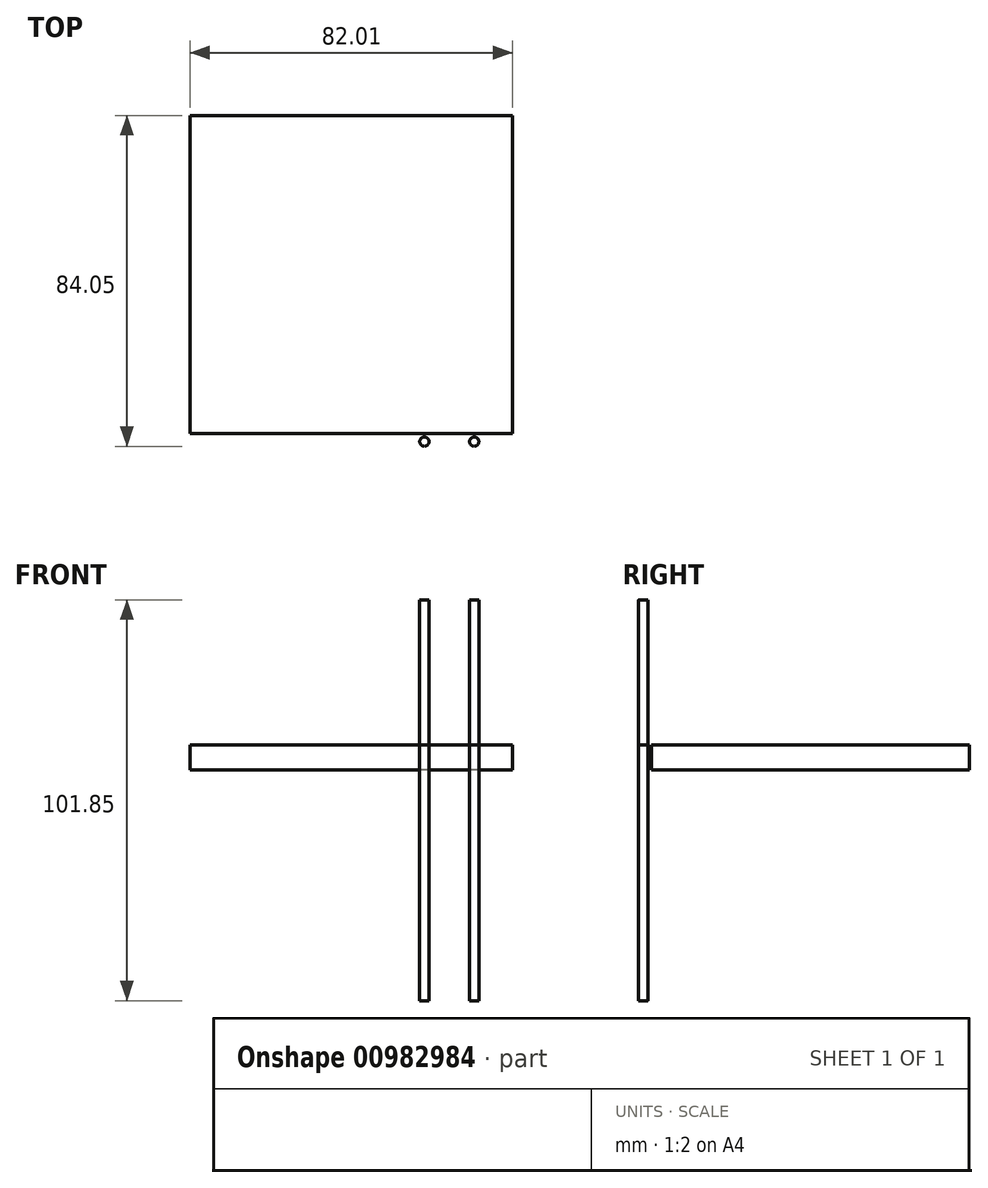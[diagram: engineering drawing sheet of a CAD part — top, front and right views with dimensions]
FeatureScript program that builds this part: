
annotation { "Feature Type Name" : "Feature", "Feature Type Description" : "" }
export const myFeature = defineFeature(function(context is Context, id is Id, definition is map)
    precondition{}
    {
        {
            var Q0;
            Q0=qCreatedBy(makeId("Top.planeOp"),FACE);
            var sketch = newSketch(context, id + "F0", { "sketchPlane" : qUnion([Q0])});
            skLineSegment(sketch, "E0.bottom", {"start": v(0, 0) * mm, "end": v(-82, 0) * mm});
            skLineSegment(sketch, "E0.top", {"start": v(0, 80.82) * mm, "end": v(-82, 80.82) * mm});
            skLineSegment(sketch, "E0.left", {"start": v(0, 0) * mm, "end": v(0, 80.82) * mm});
            skLineSegment(sketch, "E0.right", {"start": v(-82, 0) * mm, "end": v(-82, 80.82) * mm});
            skSolve(sketch);
        }
        {
            var Q0;
            Q0=makeQuery(id+"F0.imprint","IMPRINT",FACE,{"disambiguationData":[TD([[makeQuery(id+"F0.imprint","IMPRINT",EDGE,{"derivedFrom":sQuery(id+"F0.wireOp",EDGE,"E0.bottom")}),-1.0]])]});
            var sketch = newSketch(context, id + "F1", { "sketchPlane" : qUnion([Q0])});
            skCircle(sketch, "E1", {"center": v(-22.45, -2.05) * mm, "radius": 1.18 * mm});
            skCircle(sketch, "E2", {"center": v(-9.78, -2.05) * mm, "radius": 1.18 * mm});
            skSolve(sketch);
        }
        {
            var Q0;
            Q0=makeQuery(id+"F0.imprint","IMPRINT",FACE,{"disambiguationData":[TD([[makeQuery(id+"F0.imprint","IMPRINT",EDGE,{"derivedFrom":sQuery(id+"F0.wireOp",EDGE,"E0.bottom")}),-1.0]])]});
            var Q1;
            Q1=makeQuery(id+"F1.imprint","IMPRINT",FACE,{"disambiguationData":[TD([[makeQuery(id+"F1.imprint","IMPRINT",EDGE,{"derivedFrom":sQuery(id+"F1.wireOp",EDGE,"E2")}),1.0]])]});
            var Q2;
            Q2=makeQuery(id+"F1.imprint","IMPRINT",FACE,{"disambiguationData":[TD([[makeQuery(id+"F1.imprint","IMPRINT",EDGE,{"derivedFrom":sQuery(id+"F1.wireOp",EDGE,"E1")}),1.0]])]});
            extrude(context, id + "F2", {"entities" : qUnion([Q0, Q1, Q2]), "depth" : 65.02 * mm, "offsetDistance" : 25.4 * mm});
        }
        {
            var Q0;
            Q0=makeQuery(id+"F2.opExtrude","CAP_FACE",FACE,{"disambiguationData":[OSD([sQuery(id+"F0.wireOp",EDGE,"E0.bottom"),sQuery(id+"F0.wireOp",EDGE,"E0.top"),sQuery(id+"F0.wireOp",EDGE,"E0.left"),sQuery(id+"F0.wireOp",EDGE,"E0.right")])],"isStart":true});
            extrude(context, id + "F3", {"entities" : qUnion([Q0]), "operationType" : NewBodyOperationType.ADD, "oppositeDirection" : true, "depth" : 56.64 * mm, "offsetDistance" : 25.4 * mm});
        }
        {
            var Q0;
            Q0=makeQuery(id+"F2.opExtrude","CAP_FACE",FACE,{"disambiguationData":[OSD([sQuery(id+"F0.wireOp",EDGE,"E0.bottom"),sQuery(id+"F0.wireOp",EDGE,"E0.top"),sQuery(id+"F0.wireOp",EDGE,"E0.left"),sQuery(id+"F0.wireOp",EDGE,"E0.right")])],"isStart":true});
            extrude(context, id + "F4", {"entities" : qUnion([Q0]), "operationType" : NewBodyOperationType.REMOVE, "oppositeDirection" : true, "depth" : 58.67 * mm, "offsetDistance" : 25.4 * mm});
        }
        {
            var Q0;
            Q0=makeQuery(id+"F2.opExtrude","CAP_FACE",FACE,{"disambiguationData":[OSD([sQuery(id+"F1.wireOp",EDGE,"E1")])],"isStart":false});
            var Q1;
            Q1=makeQuery(id+"F2.opExtrude","CAP_FACE",FACE,{"disambiguationData":[OSD([sQuery(id+"F1.wireOp",EDGE,"E2")])],"isStart":false});
            extrude(context, id + "F5", {"entities" : qUnion([Q0, Q1]), "depth" : 36.83 * mm, "offsetDistance" : 25.4 * mm});
        }
        {
            var Q0;
            Q0=makeQuery(id+"F2.opExtrude","CAP_FACE",FACE,{"disambiguationData":[OSD([sQuery(id+"F0.wireOp",EDGE,"E0.bottom"),sQuery(id+"F0.wireOp",EDGE,"E0.top"),sQuery(id+"F0.wireOp",EDGE,"E0.left"),sQuery(id+"F0.wireOp",EDGE,"E0.right")])],"isStart":false});
            var sketch = newSketch(context, id + "F6", { "sketchPlane" : qUnion([Q0])});
            skLineSegment(sketch, "E3", {"start": v(-82, 0) * mm, "end": v(-82, 80.82) * mm});
            skLineSegment(sketch, "E4", {"start": v(-82, 80.82) * mm, "end": v(0, 80.82) * mm});
            skLineSegment(sketch, "E5", {"start": v(0, 80.82) * mm, "end": v(0, -1.79) * mm});
            skLineSegment(sketch, "E6", {"start": v(0, 0) * mm, "end": v(-7.25, 0) * mm});
            skLineSegment(sketch, "E7", {"start": v(-7.25, 0) * mm, "end": v(-7.25, 12.12) * mm});
            skLineSegment(sketch, "E8", {"start": v(-7.25, 12.12) * mm, "end": v(-26.37, 12.12) * mm});
            skLineSegment(sketch, "E9", {"start": v(-26.37, 12.12) * mm, "end": v(-26.37, 0) * mm});
            skLineSegment(sketch, "E10", {"start": v(-26.37, 0) * mm, "end": v(-82, 0) * mm});
            skSolve(sketch);
        }
    });
